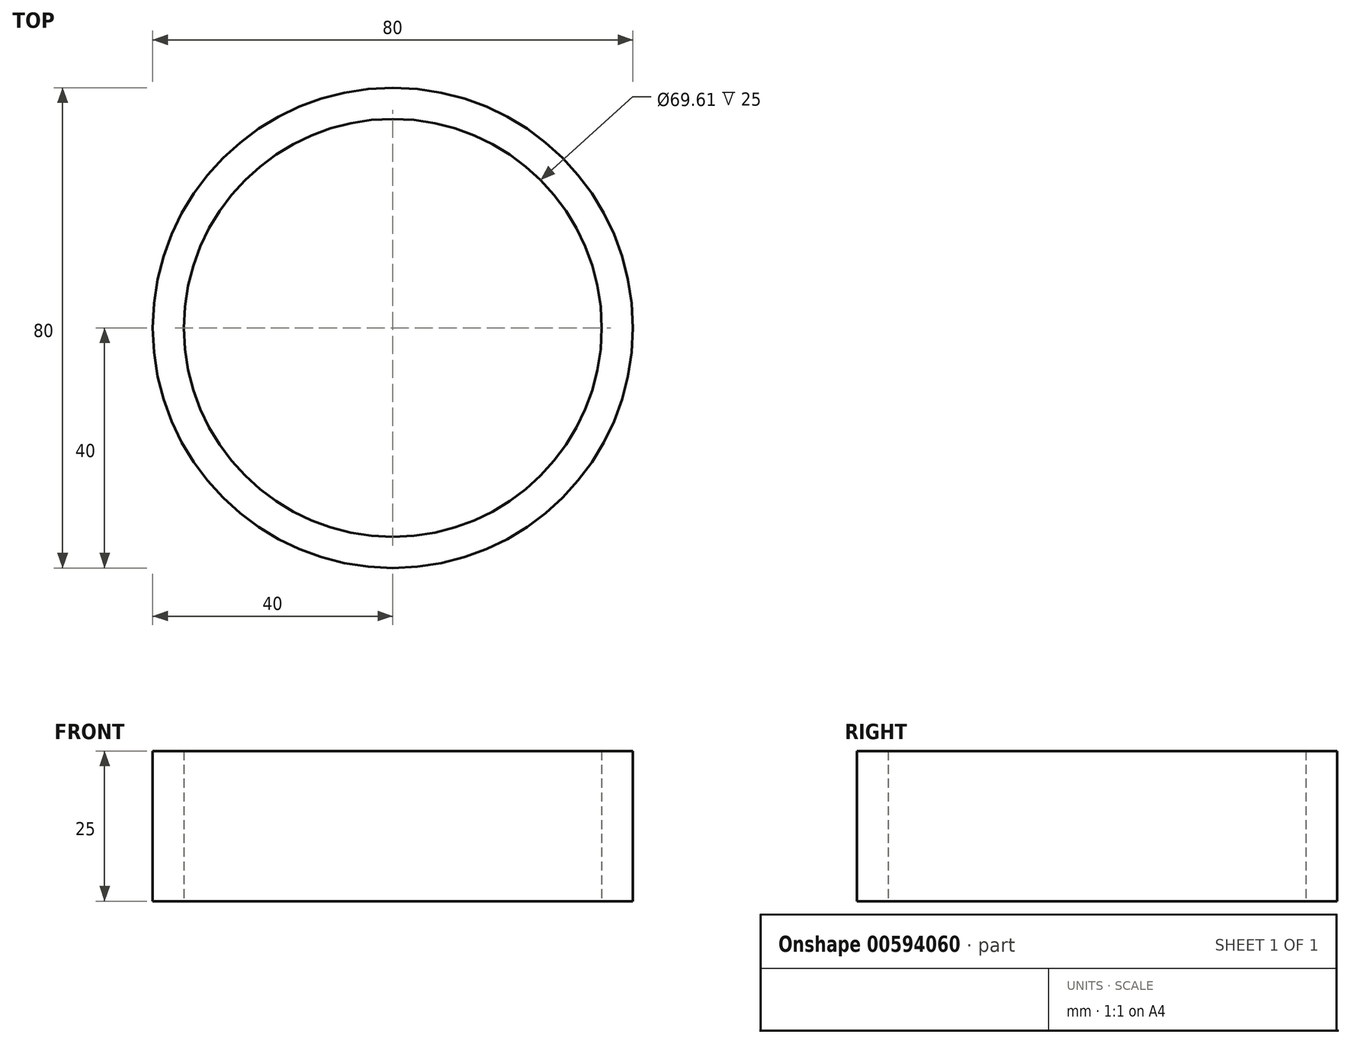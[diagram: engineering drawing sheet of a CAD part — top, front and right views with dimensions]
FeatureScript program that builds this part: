
annotation { "Feature Type Name" : "Feature", "Feature Type Description" : "" }
export const myFeature = defineFeature(function(context is Context, id is Id, definition is map)
    precondition{}
    {
        {
            var Q0;
            Q0=qCreatedBy(makeId("Top.planeOp"),FACE);
            var sketch = newSketch(context, id + "F0", { "sketchPlane" : qUnion([Q0])});
            skCircle(sketch, "E0", {"center": v(0, 0) * mm, "radius": 40 * mm});
            skSolve(sketch);
        }
        {
            var Q0;
            Q0=qCreatedBy(makeId("Top.planeOp"),FACE);
            var sketch = newSketch(context, id + "F1", { "sketchPlane" : qUnion([Q0])});
            skCircle(sketch, "E1", {"center": v(0, 0) * mm, "radius": 34.8 * mm});
            skSolve(sketch);
        }
        {
            var Q0;
            Q0 = qSketchRegion(id + "F0", true);
            extrude(context, id + "F2", {"entities" : qUnion([Q0]), "depth" : 25 * mm, "offsetDistance" : 25 * mm});
        }
        {
            var Q0;
            Q0 = qSketchRegion(id + "F1", true);
            var Q1;
            Q1=sQuery(id+"F1.wireOp",EDGE,"E1");
            extrude(context, id + "F3", {"entities" : qUnion([Q0]), "operationType" : NewBodyOperationType.REMOVE, "surfaceEntities" : qUnion([Q1]), "depth" : 103.3 * mm, "offsetDistance" : 25 * mm});
        }
    });
